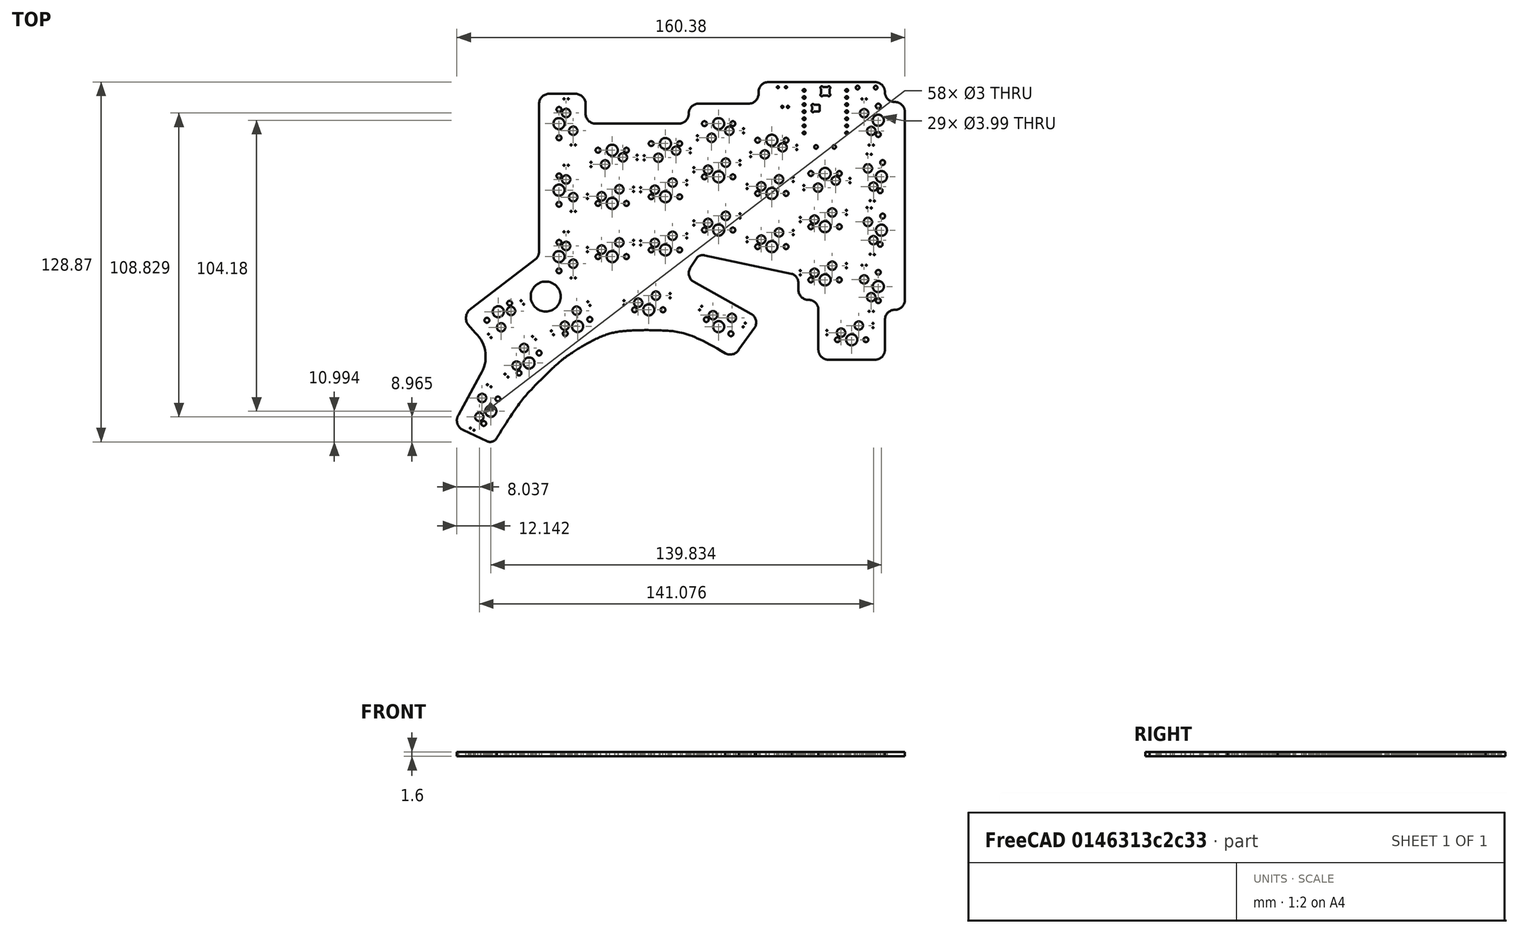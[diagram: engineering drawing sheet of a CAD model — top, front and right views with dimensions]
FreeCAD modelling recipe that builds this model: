
FCSTD DOCUMENT  (FreeCAD 0.20RUnknown)
Label: mykeep_v7a2_2023-05-16
License: All rights reserved
LicenseURL: http://en.wikipedia.org/wiki/All_rights_reserved
objects: App::Part×3, PartDesign::CoordinateSystem×1, Part::Feature×1, Sketcher::SketchObject×1
note: 3 computed .brp shape members not serialized (recipe doc carries the construction recipe); baked Part::Feature solids carry a one-line shape summary decoded from their .brp

FEATURE [PartDesign::CoordinateSystem] Local_CS_63c5
  AttacherType = Attacher::AttachEngine3D
  MapMode = 2
  Support = -> [X_Axis001]
FEATURE [Part::Feature] Pcb_63c5
  shape: bbox 160.4 x 128.9 x 1.6 mm, 358 faces (baked)
FEATURE [Sketcher::SketchObject] PCB_Sketch_63c5
  FullyConstrained = false
  sketch-geometry (97):
    g0: LineSegment StartX=25.6541 StartY=-230.551 StartZ=0 EndX=48.9601 EndY=-212.671 EndZ=0
    g1: LineSegment StartX=50.0063 StartY=-210.146 StartZ=0 EndX=50.0063 EndY=-157.227 EndZ=0
    g2: LineSegment StartX=100.013 StartY=-164.306 StartZ=0 EndX=70.2469 EndY=-164.306 EndZ=0
    g3: LineSegment StartX=28.8643 StartY=-254.286 StartZ=0 EndX=21.1251 EndY=-268.643 EndZ=0
    g4: LineSegment StartX=121.528 StartY=-245.217 StartZ=0 EndX=127.273 EndY=-237.304 EndZ=0
    g5: LineSegment StartX=22.7909 StartY=-274.007 StartZ=0 EndX=31.4693 EndY=-278.042 EndZ=0
    g6: LineSegment StartX=121.444 StartY=-157.163 StartZ=0 EndX=107.156 EndY=-157.163 EndZ=0
    g7: LineSegment StartX=153.591 StartY=-248.841 StartZ=0 EndX=170.259 EndY=-248.841 EndZ=0
    g8: LineSegment StartX=121.444 StartY=-157.163 StartZ=0 EndX=125.016 EndY=-157.163 EndZ=0
    g9: LineSegment StartX=27.1147 StartY=-239.185 StartZ=0 EndX=24.5472 EndY=-236.246 EndZ=0
    g10: LineSegment StartX=180.975 StartY=-160.139 StartZ=0 EndX=180.975 EndY=-227.41 EndZ=0
    g11: LineSegment StartX=150.019 StartY=-245.269 StartZ=0 EndX=150.019 EndY=-230.981 EndZ=0
    g12: LineSegment StartX=132.159 StartY=-149.424 StartZ=0 EndX=170.259 EndY=-149.424 EndZ=0
    g13: LineSegment StartX=173.831 StartY=-245.269 StartZ=0 EndX=173.831 EndY=-234.553 EndZ=0
    g14: LineSegment StartX=142.875 StartY=-221.456 StartZ=0 EndX=142.875 EndY=-223.838 EndZ=0
    g15: LineSegment StartX=109.301 StartY=-211.485 StartZ=0 EndX=140.433 EndY=-218.068 EndZ=0
    g16: LineSegment StartX=53.5781 StartY=-153.655 StartZ=0 EndX=63.1031 EndY=-153.655 EndZ=0
    g17: LineSegment StartX=66.675 StartY=-160.735 StartZ=0 EndX=66.6751 EndY=-157.227 EndZ=0
    g18: LineSegment StartX=105.338 StartY=-220.926 StartZ=0 EndX=125.965 EndY=-232.425 EndZ=0
    g19: LineSegment StartX=104.113 StartY=-216.025 StartZ=0 EndX=106.659 EndY=-212.138 EndZ=0
    g20: LineSegment StartX=128.588 StartY=-153.591 StartZ=0 EndX=128.588 EndY=-152.996 EndZ=0
    g21: BSplineCurve PolesCount=4 KnotsCount=2 Degree=3 IsPeriodic=0
    g22: BSplineCurve PolesCount=4 KnotsCount=2 Degree=3 IsPeriodic=0
    g23: BSplineCurve PolesCount=4 KnotsCount=2 Degree=3 IsPeriodic=0
    g24: BSplineCurve PolesCount=4 KnotsCount=2 Degree=3 IsPeriodic=0
    g25: BSplineCurve PolesCount=4 KnotsCount=2 Degree=3 IsPeriodic=0
    g26: BSplineCurve PolesCount=4 KnotsCount=2 Degree=3 IsPeriodic=0
    g27: BSplineCurve PolesCount=4 KnotsCount=2 Degree=3 IsPeriodic=0
    g28: ArcOfCircle CenterX=177.403 CenterY=-227.41 CenterZ=0 NormalX=0 NormalY=0 NormalZ=-1 AngleXU=-3.14158 Radius=3.57186 StartAngle=0 EndAngle=1.57079
    g29: ArcOfCircle CenterX=153.591 CenterY=-245.269 CenterZ=0 NormalX=0 NormalY=0 NormalZ=-1 AngleXU=-1.57082 Radius=3.57184 StartAngle=0 EndAngle=1.57083
    g30: ArcOfCircle CenterX=108.576 CenterY=-214.224 CenterZ=0 NormalX=0 NormalY=0 NormalZ=-1 AngleXU=0.827594 Radius=2.83352 StartAngle=0 EndAngle=1.00192
    g31: ArcOfCircle CenterX=46.4341 CenterY=-210.145 CenterZ=0 NormalX=0 NormalY=0 NormalZ=-1 AngleXU=-3.14155 Radius=3.57219 StartAngle=0 EndAngle=0.785327
    g32: ArcOfCircle CenterX=139.303 CenterY=-221.456 CenterZ=0 NormalX=0 NormalY=0 NormalZ=-1 AngleXU=1.89254 Radius=3.57182 StartAngle=0 EndAngle=1.24907
    g33: ArcOfCircle CenterX=177.403 CenterY=-152.996 CenterZ=0 NormalX=0 NormalY=0 NormalZ=-1 AngleXU=-1.57084 Radius=3.57176 StartAngle=0 EndAngle=1.57088
    g34: ArcOfCircle CenterX=177.403 CenterY=-234.553 CenterZ=0 NormalX=0 NormalY=0 NormalZ=-1 AngleXU=1.13645e-05 Radius=3.57197 StartAngle=0 EndAngle=1.57076
    g35: ArcOfCircle CenterX=170.26 CenterY=-152.995 CenterZ=0 NormalX=0 NormalY=0 NormalZ=-1 AngleXU=1.57076 Radius=3.5718 StartAngle=0 EndAngle=1.57085
    g36: ArcOfCircle CenterX=63.1031 CenterY=-157.227 CenterZ=0 NormalX=0 NormalY=0 NormalZ=-1 AngleXU=1.5708 Radius=3.57196 StartAngle=0 EndAngle=1.57077
    g37: ArcOfCircle CenterX=125.015 CenterY=-153.591 CenterZ=0 NormalX=0 NormalY=0 NormalZ=-1 AngleXU=-3.14155 Radius=3.57208 StartAngle=0 EndAngle=1.5707
    g38: ArcOfCircle CenterX=70.2471 CenterY=-160.734 CenterZ=0 NormalX=0 NormalY=0 NormalZ=-1 AngleXU=-1.57076 Radius=3.57204 StartAngle=0 EndAngle=1.57072
    g39: ArcOfCircle CenterX=146.447 CenterY=-230.981 CenterZ=0 NormalX=0 NormalY=0 NormalZ=-1 AngleXU=1.57078 Radius=3.57186 StartAngle=0 EndAngle=1.57082
    g40: ArcOfCircle CenterX=19.3394 CenterY=-247.738 CenterZ=0 NormalX=0 NormalY=0 NormalZ=-1 AngleXU=2.30861 Radius=11.5589 StartAngle=0 EndAngle=1.43527
    g41: ArcOfCircle CenterX=107.156 CenterY=-160.734 CenterZ=0 NormalX=0 NormalY=0 NormalZ=-1 AngleXU=-7.6573e-05 Radius=3.57165 StartAngle=0 EndAngle=1.57094
    g42: ArcOfCircle CenterX=118.435 CenterY=-243.43 CenterZ=0 NormalX=0 NormalY=0 NormalZ=-1 AngleXU=-2.61791 Radius=3.57192 StartAngle=0 EndAngle=1.57074
    g43: ArcOfCircle CenterX=27.9795 CenterY=-233.958 CenterZ=0 NormalX=0 NormalY=0 NormalZ=-1 AngleXU=-0.588033 Radius=4.12519 StartAngle=0 EndAngle=1.55998
    g44: ArcOfCircle CenterX=100.013 CenterY=-160.735 CenterZ=0 NormalX=0 NormalY=0 NormalZ=-1 AngleXU=3.14157 Radius=3.57183 StartAngle=0 EndAngle=1.57083
    g45: ArcOfCircle CenterX=107.175 CenterY=-217.863 CenterZ=0 NormalX=0 NormalY=0 NormalZ=-1 AngleXU=-1.03035 Radius=3.57193 StartAngle=0 EndAngle=1.57075
    g46: ArcOfCircle CenterX=124.179 CenterY=-235.518 CenterZ=0 NormalX=0 NormalY=0 NormalZ=-1 AngleXU=2.09441 Radius=3.57197 StartAngle=0 EndAngle=1.57076
    g47: ArcOfCircle CenterX=24.3891 CenterY=-270.57 CenterZ=0 NormalX=0 NormalY=0 NormalZ=-1 AngleXU=-1.13553 Radius=3.79045 StartAngle=0 EndAngle=1.66889
    g48: ArcOfCircle CenterX=132.16 CenterY=-152.996 CenterZ=0 NormalX=0 NormalY=0 NormalZ=-1 AngleXU=7.54118e-06 Radius=3.57195 StartAngle=0 EndAngle=1.57077
    g49: ArcOfCircle CenterX=32.5751 CenterY=-275.665 CenterZ=0 NormalX=0 NormalY=0 NormalZ=-1 AngleXU=-2.69414 Radius=2.62227 StartAngle=0 EndAngle=1.55866
    g50: ArcOfCircle CenterX=177.403 CenterY=-160.139 CenterZ=0 NormalX=0 NormalY=0 NormalZ=-1 AngleXU=1.57078 Radius=3.57186 StartAngle=0 EndAngle=1.57082
    g51: ArcOfCircle CenterX=146.447 CenterY=-223.838 CenterZ=0 NormalX=0 NormalY=0 NormalZ=-1 AngleXU=-1.57078 Radius=3.57199 StartAngle=0 EndAngle=1.57074
    g52: ArcOfCircle CenterX=170.26 CenterY=-245.269 CenterZ=0 NormalX=0 NormalY=0 NormalZ=-1 AngleXU=3.14157 Radius=3.57184 StartAngle=0 EndAngle=1.57083
    g53: ArcOfCircle CenterX=53.5782 CenterY=-157.227 CenterZ=0 NormalX=0 NormalY=0 NormalZ=-1 AngleXU=1.08866e-05 Radius=3.57196 StartAngle=0 EndAngle=1.57076
    g54: Circle CenterX=52.3875 CenterY=-226.219 CenterZ=0 NormalX=0 NormalY=0 NormalZ=1 AngleXU=0 Radius=5.35782
    g55-g58: Circle x4 (B-spline internal-alignment scaffolding for g21; pole/knot coordinates omitted)
    g59: GeomPoint X=47.0468 Y=-259.72 Z=0
    g60: GeomPoint X=34.9392 Y=-276.799 Z=0
    g61-g64: Circle x4 (B-spline internal-alignment scaffolding for g22; pole/knot coordinates omitted)
    g65: GeomPoint X=62.4749 Y=-245.928 Z=0
    g66: GeomPoint X=55.6291 Y=-251.187 Z=0
    g67-g70: Circle x4 (B-spline internal-alignment scaffolding for g23; pole/knot coordinates omitted)
    g71: GeomPoint X=72.6948 Y=-240.373 Z=0
    g72: GeomPoint X=62.4749 Y=-245.928 Z=0
    g73-g76: Circle x4 (B-spline internal-alignment scaffolding for g24; pole/knot coordinates omitted)
    g77: GeomPoint X=116.649 Y=-246.524 Z=0
    g78: GeomPoint X=96.1103 Y=-238.487 Z=0
    g79-g82: Circle x4 (B-spline internal-alignment scaffolding for g25; pole/knot coordinates omitted)
    g83: GeomPoint X=83.0133 Y=-238.388 Z=0
    g84: GeomPoint X=72.6948 Y=-240.373 Z=0
    g85-g88: Circle x4 (B-spline internal-alignment scaffolding for g26; pole/knot coordinates omitted)
    g89: GeomPoint X=55.6291 Y=-251.187 Z=0
    g90: GeomPoint X=47.0468 Y=-259.72 Z=0
    g91-g94: Circle x4 (B-spline internal-alignment scaffolding for g27; pole/knot coordinates omitted)
    g95: GeomPoint X=96.1103 Y=-238.487 Z=0
    g96: GeomPoint X=83.0133 Y=-238.388 Z=0
  constraints (61):
    c: Coincident(g3,g47)
    c: Coincident(g5,g47)
    c: Coincident(g9,g43)
    c: Coincident(g0,g43)
    c: Coincident(g9,g40)
    c: Coincident(g3,g40)
    c: Coincident(g5,g49)
    c: Coincident(g21,g49)
    c: Coincident(g21,g26)
    c: Coincident(g0,g31)
    c: Coincident(g1,g31)
    c: Coincident(g1,g53)
    c: Coincident(g16,g53)
    c: Coincident(g22,g26)
    c: Coincident(g22,g23)
    c: Coincident(g16,g36)
    c: Coincident(g17,g38)
    c: Coincident(g17,g36)
    c: Coincident(g2,g38)
    c: Coincident(g23,g25)
    c: Coincident(g25,g27)
    c: Coincident(g24,g27)
    c: Coincident(g2,g44)
    c: Coincident(g41,g44)
    c: Coincident(g19,g45)
    c: Coincident(g18,g45)
    c: Coincident(g19,g30)
    c: Coincident(g6,g41)
    c: Coincident(g15,g30)
    c: Coincident(g24,g42)
    c: Coincident(g6,g8)
    c: Coincident(g4,g42)
    c: Coincident(g8,g37)
    c: Coincident(g18,g46)
    c: Coincident(g4,g46)
    c: Coincident(g20,g37)
    c: Coincident(g20,g48)
    c: Coincident(g12,g48)
    c: Coincident(g15,g32)
    c: Coincident(g14,g51)
    c: Coincident(g14,g32)
    c: Coincident(g39,g51)
    c: Coincident(g11,g29)
    c: Coincident(g11,g39)
    c: Coincident(g7,g29)
    c: Coincident(g7,g52)
    c: Coincident(g12,g35)
    c: Coincident(g13,g52)
    c: Coincident(g13,g34)
    c: Coincident(g33,g35)
    c: Coincident(g28,g34)
    c: Coincident(g33,g50)
    c: Coincident(g10,g28)
    c: Coincident(g10,g50)
    c: InternalAlignment(g55-g60 -> g21) x6
    c: InternalAlignment(g61-g66 -> g22) x6
    c: InternalAlignment(g67-g72 -> g23) x6
    c: InternalAlignment(g73-g78 -> g24) x6
    c: InternalAlignment(g79-g84 -> g25) x6
    c: InternalAlignment(g85-g90 -> g26) x6
    c: InternalAlignment(g91-g96 -> g27) x6
FEATURE [App::Part] Board_Geoms_63c5
  Group = -> [Pcb_63c5,PCB_Sketch_63c5]
  Origin = -> Origin
FEATURE [App::Part] Step_Models_63c5
  Origin = -> Origin002
FEATURE [App::Part] Board_63c5  label="mykeeb_v7a2"
  Group = -> [Local_CS_63c5,Board_Geoms_63c5,Step_Models_63c5]
  Origin = -> Origin001
